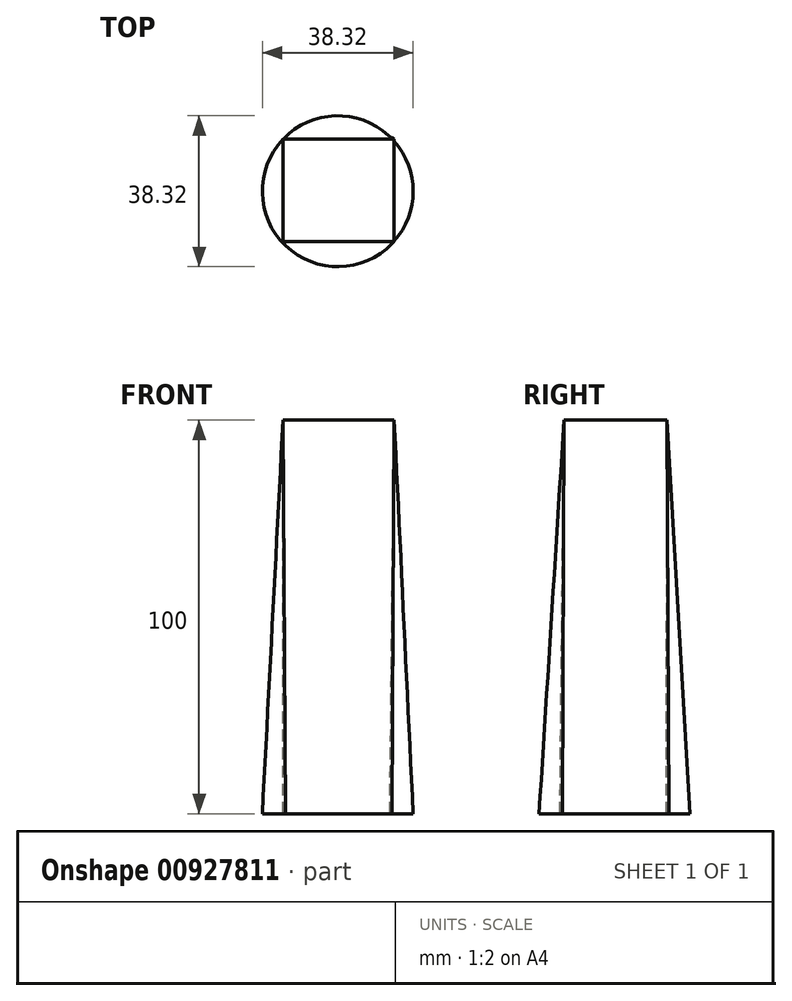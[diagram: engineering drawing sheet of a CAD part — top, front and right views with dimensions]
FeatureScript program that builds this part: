
annotation { "Feature Type Name" : "Feature", "Feature Type Description" : "" }
export const myFeature = defineFeature(function(context is Context, id is Id, definition is map)
    precondition{}
    {
        {
            var Q0;
            Q0=qCreatedBy(makeId("Top.planeOp"),FACE);
            cPlane(context, id + "F0", {"entities" : qUnion([Q0]), "cplaneType" : CPlaneType.OFFSET, "offset" : 100 * mm, "width" : 150 * mm, "height" : 150 * mm});
        }
        {
            var Q0;
            Q0=qCreatedBy(id+"F0.planeOp",FACE);
            var sketch = newSketch(context, id + "F1", { "sketchPlane" : qUnion([Q0])});
            skLineSegment(sketch, "E0.bottom", {"start": v(-13.88, 13.28) * mm, "end": v(14.34, 13.28) * mm});
            skLineSegment(sketch, "E0.top", {"start": v(-13.88, -12.82) * mm, "end": v(14.34, -12.82) * mm});
            skLineSegment(sketch, "E0.left", {"start": v(-13.88, 13.28) * mm, "end": v(-13.88, -12.82) * mm});
            skLineSegment(sketch, "E0.right", {"start": v(14.34, 13.28) * mm, "end": v(14.34, -12.82) * mm});
            skSolve(sketch);
        }
        {
            var Q0;
            Q0=qCreatedBy(makeId("Top.planeOp"),FACE);
            var sketch = newSketch(context, id + "F2", { "sketchPlane" : qUnion([Q0])});
            skCircle(sketch, "E1", {"center": v(0, 0) * mm, "radius": 19.16 * mm});
            skSolve(sketch);
        }
        {
            var Q0;
            Q0=makeQuery(id+"F2.imprint","IMPRINT",FACE,{"disambiguationData":[TD([[makeQuery(id+"F2.imprint","IMPRINT",EDGE,{"derivedFrom":sQuery(id+"F2.wireOp",EDGE,"E1")}),1.0]])]});
            var Q1;
            Q1=makeQuery(id+"F1.imprint","IMPRINT",FACE,{"disambiguationData":[TD([[makeQuery(id+"F1.imprint","IMPRINT",EDGE,{"derivedFrom":sQuery(id+"F1.wireOp",EDGE,"E0.bottom")}),-1.0]])]});
            loft(context, id + "F3", {"sheetProfilesArray" : [{ "sheetProfileEntities" : qUnion([Q0]) }, { "sheetProfileEntities" : qUnion([Q1]) }]});
        }
    });
